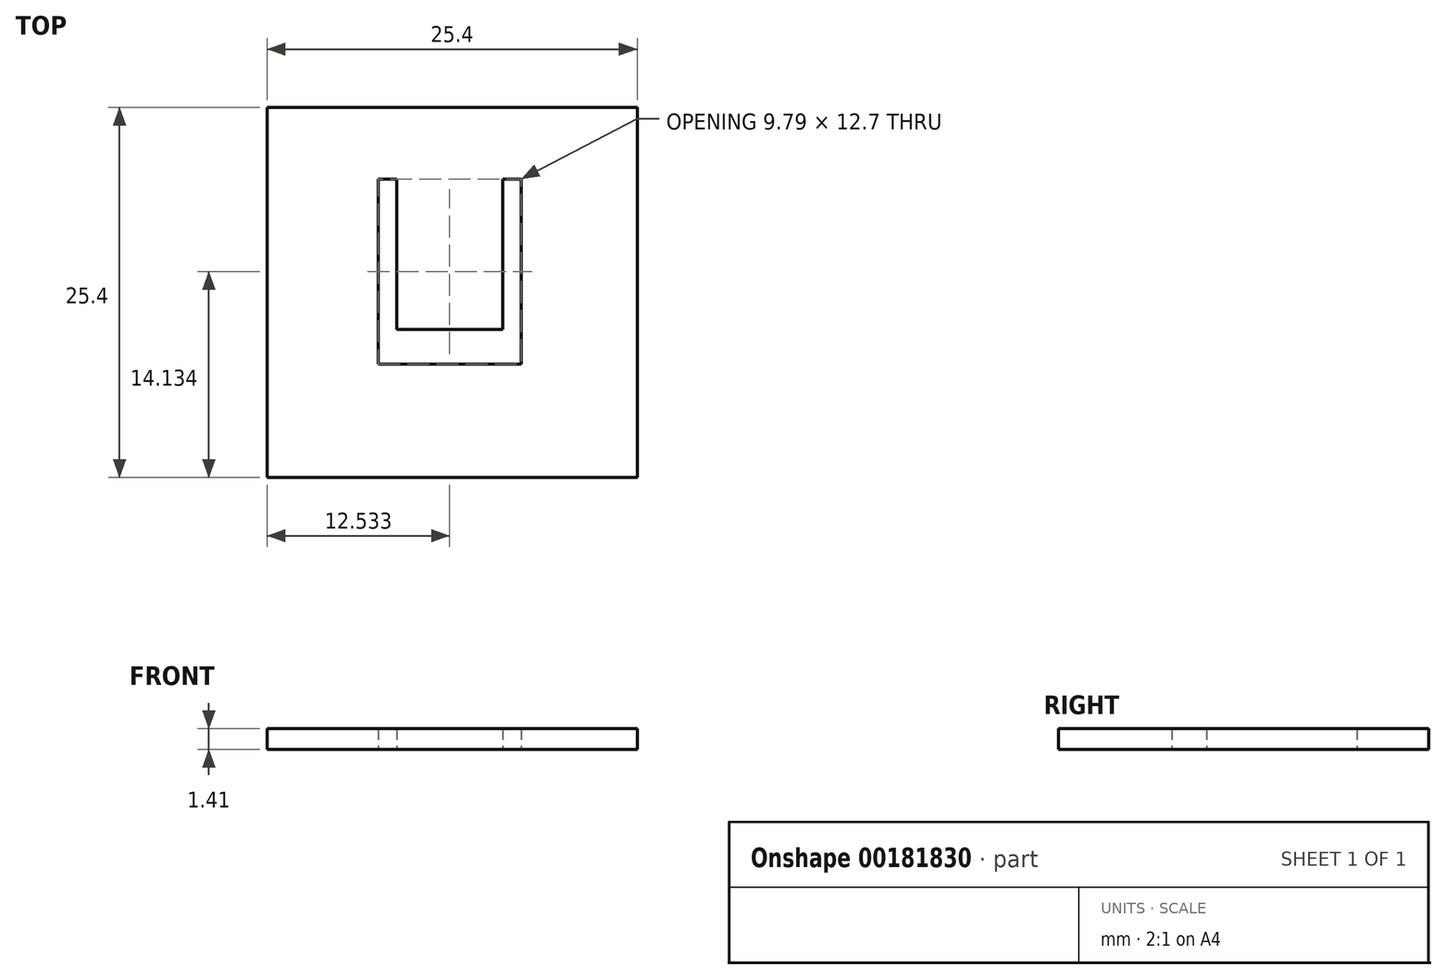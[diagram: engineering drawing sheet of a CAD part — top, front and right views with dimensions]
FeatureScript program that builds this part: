
annotation { "Feature Type Name" : "Feature", "Feature Type Description" : "" }
export const myFeature = defineFeature(function(context is Context, id is Id, definition is map)
    precondition{}
    {
        {
            var Q0;
            Q0=qCreatedBy(makeId("Top.planeOp"),FACE);
            var sketch = newSketch(context, id + "F0", { "sketchPlane" : qUnion([Q0])});
            skLineSegment(sketch, "E0.bottom", {"start": v(0, 0) * mm, "end": v(25.4, 0) * mm});
            skLineSegment(sketch, "E0.top", {"start": v(0, 25.4) * mm, "end": v(25.4, 25.4) * mm});
            skLineSegment(sketch, "E0.left", {"start": v(0, 0) * mm, "end": v(0, 25.4) * mm});
            skLineSegment(sketch, "E0.right", {"start": v(25.4, 0) * mm, "end": v(25.4, 25.4) * mm});
            skLineSegment(sketch, "E1", {"start": v(7.64, 20.48) * mm, "end": v(7.64, 7.78) * mm});
            skLineSegment(sketch, "E2", {"start": v(7.64, 7.78) * mm, "end": v(17.43, 7.78) * mm});
            skLineSegment(sketch, "E3", {"start": v(17.43, 7.78) * mm, "end": v(17.43, 20.48) * mm});
            skLineSegment(sketch, "E4", {"start": v(17.43, 20.48) * mm, "end": v(16.16, 20.48) * mm});
            skLineSegment(sketch, "E5", {"start": v(16.16, 20.48) * mm, "end": v(16.16, 10.15) * mm});
            skLineSegment(sketch, "E6", {"start": v(16.16, 10.15) * mm, "end": v(8.9, 10.15) * mm});
            skLineSegment(sketch, "E7", {"start": v(8.9, 10.15) * mm, "end": v(8.9, 20.48) * mm});
            skLineSegment(sketch, "E8", {"start": v(8.9, 20.48) * mm, "end": v(7.64, 20.48) * mm});
            skSolve(sketch);
        }
        {
            var Q0;
            Q0 = qSketchRegion(id + "F0", true);
            extrude(context, id + "F1", {"entities" : qUnion([Q0]), "depth" : 1.41 * mm});
        }
    });
